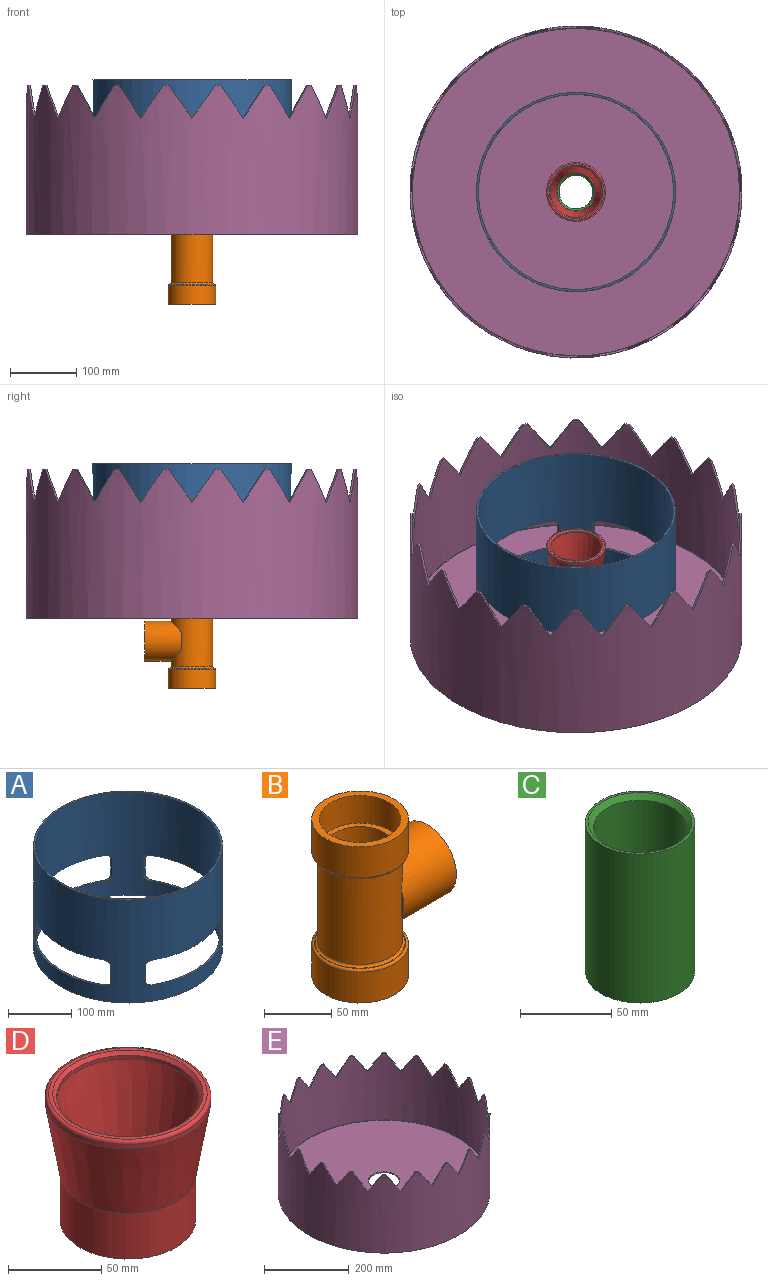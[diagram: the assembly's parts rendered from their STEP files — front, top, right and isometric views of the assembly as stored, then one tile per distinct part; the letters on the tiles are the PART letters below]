
ASSEMBLY  parts=5 mates=4
PART A: 36 faces, bbox 300x300x200 mm
  f0: plane 150x23.57mm, normal (0,0,-1), area 471.7mm2, adj f9,f15,f16,f17
  f1: cylinder r=10mm len=10mm, axis (1,0,0), area 56.4mm2, adj f2,f8,f16,f17
  f2: plane 30x3.66mm, normal (0,1,0), area 109.8mm2, adj f1,f3,f16,f17
  f3: cylinder r=10mm len=10mm, axis (1,0,0), area 56.4mm2, adj f2,f12,f16,f17
  f4: plane 150x23.57mm, normal (0,0,1), area 471.7mm2, adj f11,f13,f16,f17
  f5: cylinder r=10mm len=10mm, axis (1,0,0), area 56.4mm2, adj f6,f12,f16,f17
  f6: plane 30x3.66mm, normal (0,-1,0), area 109.8mm2, adj f5,f7,f16,f17
  f7: cylinder r=10mm len=10mm, axis (1,0,0), area 56.4mm2, adj f6,f8,f16,f17
  f8: plane 150x23.57mm, normal (0,0,-1), area 471.7mm2, adj f1,f7,f16,f17
  f9: cylinder r=10mm len=10mm, axis (1,0,0), area 56.4mm2, adj f0,f10,f16,f17
  f10: plane 30x3.66mm, normal (0,1,0), area 109.8mm2, adj f9,f11,f16,f17
  f11: cylinder r=10mm len=10mm, axis (1,0,0), area 56.4mm2, adj f4,f10,f16,f17
  f12: plane 150x23.57mm, normal (0,0,1), area 471.7mm2, adj f3,f5,f16,f17
  f13: cylinder r=10mm len=10mm, axis (1,0,0), area 56.4mm2, adj f4,f14,f16,f17
  f14: plane 30x3.66mm, normal (0,-1,0), area 109.8mm2, adj f13,f15,f16,f17
  f15: cylinder r=10mm len=10mm, axis (1,0,0), area 56.4mm2, adj f0,f14,f16,f17
  f16: cylinder r=147mm len=294mm, axis (0,0,-1), area 148887.5mm2, adj f0,f1,f2,f3,f4,f5,f6,f7
  f17: cylinder r=150mm len=300mm, axis (0,0,-1), area 152760mm2, adj f0,f1,f2,f3,f4,f5,f6,f7
  f18: plane 300x300mm, normal (0,0,1), area 2799.2mm2, adj f16,f17
  f19: plane 300x300mm, normal (0,0,-1), area 2799.2mm2, adj f16,f17
  f20: cylinder r=10mm len=10mm, axis (0,-1,0), area 56.4mm2, adj f16,f17,f21,f27
  f21: plane 30x3.66mm, normal (-1,0,0), area 109.8mm2, adj f16,f17,f20,f22
  f22: cylinder r=10mm len=10mm, axis (0,-1,0), area 56.4mm2, adj f16,f17,f21,f23
  f23: plane 150x23.57mm, normal (0,0,1), area 471.7mm2, adj f16,f17,f22,f24
  f24: cylinder r=10mm len=10mm, axis (0,-1,0), area 56.4mm2, adj f16,f17,f23,f25
  f25: plane 30x3.66mm, normal (1,0,0), area 109.8mm2, adj f16,f17,f24,f26
  f26: cylinder r=10mm len=10mm, axis (0,-1,0), area 56.4mm2, adj f16,f17,f25,f27
  f27: plane 150x23.57mm, normal (0,0,-1), area 471.7mm2, adj f16,f17,f20,f26
  f28: plane 150x23.57mm, normal (0,0,-1), area 471.7mm2, adj f16,f17,f29,f35
  f29: cylinder r=10mm len=10mm, axis (0,-1,0), area 56.4mm2, adj f16,f17,f28,f30
  f30: plane 30x3.66mm, normal (1,0,0), area 109.8mm2, adj f16,f17,f29,f31
  f31: cylinder r=10mm len=10mm, axis (0,-1,0), area 56.4mm2, adj f16,f17,f30,f32
  f32: plane 150x23.57mm, normal (0,0,1), area 471.7mm2, adj f16,f17,f31,f33
  f33: cylinder r=10mm len=10mm, axis (0,-1,0), area 56.4mm2, adj f16,f17,f32,f34
  f34: plane 30x3.66mm, normal (-1,0,0), area 109.8mm2, adj f16,f17,f33,f35
  f35: cylinder r=10mm len=10mm, axis (0,-1,0), area 56.4mm2, adj f16,f17,f28,f34
PART B: 23 faces, bbox 110x77.9x142 mm
  f0: plane 68x68mm, normal (0,0,1), area 106mm2, adj f20,f21
  f1: cylinder r=31.5mm len=78mm, axis (0,0,-1), area 12224.6mm2, adj f12,f13,f14,f21,f22
  f2: plane 68x68mm, normal (0,0,-1), area 106mm2, adj f19,f22
  f3: cylinder r=36mm len=72mm, axis (0,0,-1), area 6333.5mm2, adj f4,f19
  f4: plane 72x72mm, normal (0,0,1), area 1206.2mm2, adj f3,f5
  f5: cylinder r=30.2mm len=60.4mm, axis (0,0,-1), area 4743.8mm2, adj f4,f6
  f6: plane 60.4x60.4mm, normal (0,0,1), area 822.4mm2, adj f5,f7
  f7: cylinder r=25.5mm len=92mm, axis (0,0,-1), area 13353.3mm2, adj f6,f8,f15
  f8: plane 60.4x60.4mm, normal (0,0,-1), area 822.4mm2, adj f7,f9
  f9: cylinder r=30.2mm len=60.4mm, axis (0,0,-1), area 4743.8mm2, adj f8,f10
  f10: plane 72x72mm, normal (0,0,-1), area 1206.2mm2, adj f9,f11
  f11: cylinder r=36mm len=72mm, axis (0,0,-1), area 6333.5mm2, adj f10,f20
  f12: cylinder r=30.2mm len=60.4mm, axis (1,0,0), area 9100.9mm2, adj f1,f13,f14,f16
  f13: plane 26.08x2.96mm, normal (-1,0,0), area 52mm2, adj f1,f12
  f14: plane 26.08x2.96mm, normal (-1,0,0), area 52mm2, adj f1,f12
  f15: cylinder r=20mm len=40mm, axis (1,0,0), area 3148.3mm2, adj f7,f17
  f16: plane 60.4x60.4mm, normal (1,0,0), area 1025.4mm2, adj f12,f18
  f17: plane 48.4x48.4mm, normal (1,0,0), area 583.2mm2, adj f15,f18
  f18: cylinder r=24.2mm len=48.4mm, axis (1,0,0), area 3801.3mm2, adj f16,f17
  f19: torus R=34mm, axis (0,0,1), area 696.3mm2, adj f2,f3
  f20: torus R=34mm, axis (0,0,-1), area 696.3mm2, adj f0,f11
  f21: torus R=33.5mm, axis (0,0,-1), area 636.1mm2, adj f0,f1
  f22: torus R=33.5mm, axis (0,0,1), area 636.1mm2, adj f1,f2
PART C: 6 faces, bbox 60x60x100 mm
  f0: cylinder r=25.5mm len=94mm, axis (0,0,-1), area 15060.8mm2, adj f4,f5
  f1: cylinder r=30mm len=100mm, axis (0,0,-1), area 18849.6mm2, adj f2,f3
  f2: plane 60x60mm, normal (0,0,1), area 275.7mm2, adj f1,f4
  f3: plane 60x60mm, normal (0,0,-1), area 275.7mm2, adj f1,f5
  f4: cone r=25.5mm half-angle=45deg, axis (0,0,1), area 719.7mm2, adj f0,f2
  f5: cone r=28.5mm half-angle=45deg, axis (0,0,-1), area 719.7mm2, adj f0,f3
PART D: 11 faces, bbox 96.3x96.3x83 mm
  f0: plane 85x85mm, normal (0,0,1), area 572.3mm2, adj f9,f10
  f1: cylinder r=38.3mm len=76.6mm, axis (0,0,-1), area 596.9mm2, adj f2,f10
  f2: cone r=29.27mm half-angle=9.6deg, axis (0,0,1), area 11521.4mm2, adj f1,f3
  f3: plane 60.4x60.4mm, normal (0,0,-1), area 174mm2, adj f2,f4
  f4: cylinder r=30.2mm len=60.4mm, axis (0,0,-1), area 4743.8mm2, adj f3,f5
  f5: plane 72.8x72.8mm, normal (0,0,-1), area 1297.2mm2, adj f4,f6
  f6: cylinder r=36.4mm len=72.8mm, axis (0,0,-1), area 6861.2mm2, adj f5,f7
  f7: cone r=36.4mm half-angle=9.6deg, axis (0,0,1), area 12371.9mm2, adj f6,f8
  f8: cylinder r=44.5mm len=89mm, axis (0,0,-1), area 838.8mm2, adj f7,f9
  f9: torus R=42.5mm, axis (0,0,-1), area 864mm2, adj f0,f8
  f10: cone r=40.3mm half-angle=45deg, axis (0,0,1), area 698.4mm2, adj f0,f1
PART E: 69 faces, bbox 500x500x225 mm
  f0: cylinder r=247mm len=494mm, axis (0,0,-1), area 45782.4mm2, adj f61,f67
  f1: plane 8.19x4.18mm, normal (0,0,1), area 23.4mm2, adj f2,f58,f59,f63
  f2: plane 50x34.99mm, normal (0.78,-0.25,0.57), area 183.7mm2, adj f1,f3,f58,f59
  f3: plane 50x33.46mm, normal (-0.78,0.25,0.57), area 183.7mm2, adj f2,f4,f58,f59
  f4: plane 8.32x6.21mm, normal (0,0,1), area 23.4mm2, adj f3,f5,f58,f59
  f5: plane 50x31.55mm, normal (0.66,-0.48,0.57), area 183.7mm2, adj f4,f6,f58,f59
  f6: plane 50x28.64mm, normal (-0.66,0.48,0.57), area 183.7mm2, adj f5,f7,f58,f59
  f7: plane 7.64x7.64mm, normal (0,0,1), area 23.4mm2, adj f6,f8,f58,f59
  f8: plane 50x28.64mm, normal (0.48,-0.66,0.57), area 183.7mm2, adj f7,f9,f58,f59
  f9: plane 50x31.55mm, normal (-0.48,0.66,0.57), area 183.7mm2, adj f8,f10,f58,f59
  f10: plane 8.32x6.21mm, normal (0,0,1), area 23.4mm2, adj f9,f11,f58,f59
  f11: plane 50x33.46mm, normal (0.25,-0.78,0.57), area 183.7mm2, adj f10,f12,f58,f59
  f12: plane 50x34.99mm, normal (-0.25,0.78,0.57), area 183.7mm2, adj f11,f13,f58,f59
  f13: plane 8.19x4.18mm, normal (0,0,1), area 23.4mm2, adj f12,f14,f58,f59
  f14: plane 50x35.01mm, normal (0,-0.82,0.57), area 183.7mm2, adj f13,f15,f58,f59
  f15: plane 50x35.01mm, normal (0,0.82,0.57), area 183.7mm2, adj f14,f16,f58,f59
  f16: plane 8.19x4.18mm, normal (0,0,1), area 23.4mm2, adj f15,f17,f58,f59
  f17: plane 50x34.99mm, normal (-0.25,-0.78,0.57), area 183.7mm2, adj f16,f18,f58,f59
  f18: plane 50x33.46mm, normal (0.25,0.78,0.57), area 183.7mm2, adj f17,f19,f58,f59
  f19: plane 8.32x6.21mm, normal (0,0,1), area 23.4mm2, adj f18,f20,f58,f59
  f20: plane 50x31.55mm, normal (-0.48,-0.66,0.57), area 183.7mm2, adj f19,f21,f58,f59
  f21: plane 50x28.64mm, normal (0.48,0.66,0.57), area 183.7mm2, adj f20,f22,f58,f59
  f22: plane 7.64x7.64mm, normal (0,0,1), area 23.4mm2, adj f21,f23,f58,f59
  f23: plane 50x28.64mm, normal (-0.66,-0.48,0.57), area 183.7mm2, adj f22,f24,f58,f59
  f24: plane 50x31.55mm, normal (0.66,0.48,0.57), area 183.7mm2, adj f23,f25,f58,f59
  f25: plane 8.32x6.21mm, normal (0,0,1), area 23.4mm2, adj f24,f26,f58,f59
  f26: plane 50x33.46mm, normal (-0.78,-0.25,0.57), area 183.7mm2, adj f25,f27,f58,f59
  f27: plane 50x34.99mm, normal (0.78,0.25,0.57), area 183.7mm2, adj f26,f28,f58,f59
  f28: plane 8.19x4.18mm, normal (0,0,1), area 23.4mm2, adj f27,f29,f58,f59
  f29: plane 50x35.01mm, normal (-0.82,0,0.57), area 183.7mm2, adj f28,f30,f58,f59
  f30: plane 50x35.01mm, normal (0.82,0,0.57), area 183.7mm2, adj f29,f31,f58,f59
  f31: plane 8.19x4.18mm, normal (0,0,1), area 23.4mm2, adj f30,f32,f58,f59
  f32: plane 50x34.99mm, normal (-0.78,0.25,0.57), area 183.7mm2, adj f31,f33,f58,f59
  f33: plane 50x33.46mm, normal (0.78,-0.25,0.57), area 183.7mm2, adj f32,f34,f58,f59
  f34: plane 8.32x6.21mm, normal (0,0,1), area 23.4mm2, adj f33,f35,f58,f59
  f35: plane 50x31.55mm, normal (-0.66,0.48,0.57), area 183.7mm2, adj f34,f36,f58,f59
  f36: plane 50x28.64mm, normal (0.66,-0.48,0.57), area 183.7mm2, adj f35,f37,f58,f59
  f37: plane 7.64x7.64mm, normal (0,0,1), area 23.4mm2, adj f36,f38,f58,f59
  f38: plane 50x28.64mm, normal (-0.48,0.66,0.57), area 183.7mm2, adj f37,f39,f58,f59
  f39: plane 50x31.55mm, normal (0.48,-0.66,0.57), area 183.7mm2, adj f38,f40,f58,f59
  f40: plane 8.32x6.21mm, normal (0,0,1), area 23.4mm2, adj f39,f41,f58,f59
  f41: plane 50x33.46mm, normal (-0.25,0.78,0.57), area 183.7mm2, adj f40,f42,f58,f59
  f42: plane 50x34.99mm, normal (0.25,-0.78,0.57), area 183.7mm2, adj f41,f43,f58,f59
  f43: plane 8.19x4.18mm, normal (0,0,1), area 23.4mm2, adj f42,f44,f58,f59
  f44: plane 50x35.01mm, normal (0,0.82,0.57), area 183.7mm2, adj f43,f45,f58,f59
  f45: plane 50x35.01mm, normal (0,-0.82,0.57), area 183.7mm2, adj f44,f46,f58,f59
  f46: plane 8.19x4.18mm, normal (0,0,1), area 23.4mm2, adj f45,f47,f58,f59
  f47: plane 50x34.99mm, normal (0.25,0.78,0.57), area 183.7mm2, adj f46,f48,f58,f59
  f48: plane 50x33.46mm, normal (-0.25,-0.78,0.57), area 183.7mm2, adj f47,f49,f58,f59
  f49: plane 8.32x6.21mm, normal (0,0,1), area 23.4mm2, adj f48,f50,f58,f59
  f50: plane 50x31.55mm, normal (0.48,0.66,0.57), area 183.7mm2, adj f49,f51,f58,f59
  f51: plane 50x28.64mm, normal (-0.48,-0.66,0.57), area 183.7mm2, adj f50,f52,f58,f59
  f52: plane 7.64x7.64mm, normal (0,0,1), area 23.4mm2, adj f51,f53,f58,f59
  f53: plane 50x28.64mm, normal (0.66,0.48,0.57), area 183.7mm2, adj f52,f54,f58,f59
  f54: plane 50x31.55mm, normal (-0.66,-0.48,0.57), area 183.7mm2, adj f53,f55,f58,f59
  f55: plane 8.32x6.21mm, normal (0,0,1), area 23.4mm2, adj f54,f56,f58,f59
  f56: plane 50x33.46mm, normal (0.78,0.25,0.57), area 183.7mm2, adj f55,f57,f58,f59
  f57: plane 50x34.99mm, normal (-0.78,-0.25,0.57), area 183.7mm2, adj f56,f58,f59,f60
  f58: cylinder r=247mm len=494mm, axis (0,0,-1), area 262128.5mm2, adj f1,f2,f3,f4,f5,f6,f7,f8
  f59: cylinder r=250mm len=500mm, axis (0,0,-1), area 318361.2mm2, adj f1,f2,f3,f4,f5,f6,f7,f8
  f60: plane 8.19x4.18mm, normal (0,0,1), area 23.4mm2, adj f57,f58,f59,f62
  f61: plane 500x500mm, normal (0,0,-1), area 4684.1mm2, adj f0,f59
  f62: plane 50x35.01mm, normal (0.82,0,0.57), area 183.7mm2, adj f58,f59,f60,f63
  f63: plane 50x35.01mm, normal (-0.82,0,0.57), area 183.7mm2, adj f1,f58,f59,f62
  f64: plane 493x493mm, normal (0,0,-1), area 186818.7mm2, adj f67,f68
  f65: plane 493x493mm, normal (0,0,1), area 186818.7mm2, adj f66,f68
  f66: cone r=246.5mm half-angle=45deg, axis (0,0,1), area 1096.3mm2, adj f58,f65
  f67: cone r=247mm half-angle=45deg, axis (0,0,-1), area 1096.3mm2, adj f0,f64
  f68: cylinder r=36mm len=72mm, axis (0,0,-1), area 678.6mm2, adj f64,f65
PLACE A t=(-59.72,31.1,-21.14)mm
PLACE B rot(axis=(0,0,1),90deg) t=(-59.72,31.1,-159.14)mm
PLACE C t=(-59.72,31.1,-42.14)mm
PLACE D t=(-59.72,31.1,32.86)mm
PLACE E t=(-59.72,31.1,-54.14)mm
MATE fastened A.f16 <-> E.f0  axis (0,0,-1) through (-59.72,31.1,-21.14)mm
MATE fastened C.f1 <-> D.f1  axis (0,0,1) through (-59.72,31.1,57.86)mm
MATE fastened D.f1 <-> E.f0  axis (0,0,1) through (-59.72,31.1,115.86)mm
MATE fastened B.f1 <-> C.f0  axis (0,0,1) through (-59.72,31.1,-42.14)mm
